# Revit family: Storage_Cabinets-Teknion-RHSS_Standard Storage_Cabinet-R2018
name_source: partatom
category: Furniture
revit_build: Autodesk Revit 2018 (Build: 20170223_1515(x64)
units: mm (PartAtom-declared; Revit-internal decimal feet)

## family parameters
Always vertical = Yes
Cut with Voids When Loaded = No
OmniClass Number = 23.40.20.00
OmniClass Title = General Furniture and Specialties
Room Calculation Point = No
Shared = Yes
Work Plane-Based = No

## types (7) — shared parameters
Assembly Code = E2020200
Manufacturer = Teknion
Manufacturer Fax = 416.661.4586
Part Number = RHSS
Product Documentation Link = https://www.teknion.com
Product Line = Modular Cabinets
Product Page URL = https://www.teknion.com
Series = Modular Cabinets
Sustainability Data = https://www.teknion.com
URL = www.teknion.com
Unit Weight URL = http://www.teknion.com
Warranty = http://www.teknion.com

## per-type parameters (varying)
| type | Description | Model | No Door | Width | With Doors |
| With Doors, 24" Depth, 24" Width | Standard Storage Cabinet, 24"Depth, 24" Width, With Doors | RHSSD2424__ | No | 24 " | Yes |
| No Door, 24" Depth, 12" Width | Standard Storage Cabinet, 24"Depth, 12"Width, No Door | RHSSO2412__ | Yes | 12 " | No |
| With Doors, 24" Depth, 30" Width | Standard Storage Cabinet, 24"Depth, 30" Width, With Doors | RHSSD2430__ | No | 30 " | Yes |
| With Doors, 24" Depth, 36" Width | Standard Storage Cabinet, 24"Depth, 36" Width, With Doors | RHSSD2436__ | No | 36 " | Yes |
| No Door, 24" Depth, 24" Width | Standard Storage Cabinet, 24"Depth, 24"Width, No Door | RHSSO2424__ | Yes | 24 " | No |
| No Door, 24" Depth, 30" Width | Standard Storage Cabinet, 24"Depth, 30"Width, No Door | RHSSO2430__ | Yes | 30 " | No |
| No Door, 24" Depth, 36" Width | Standard Storage Cabinet, 24"Depth, 36"Width, No Door | RHSSO2436__ | Yes | 36 " | No |

## geometry (parser evidence)
native form markers: Sweep x3
no freeform markers — native parametric forms only
